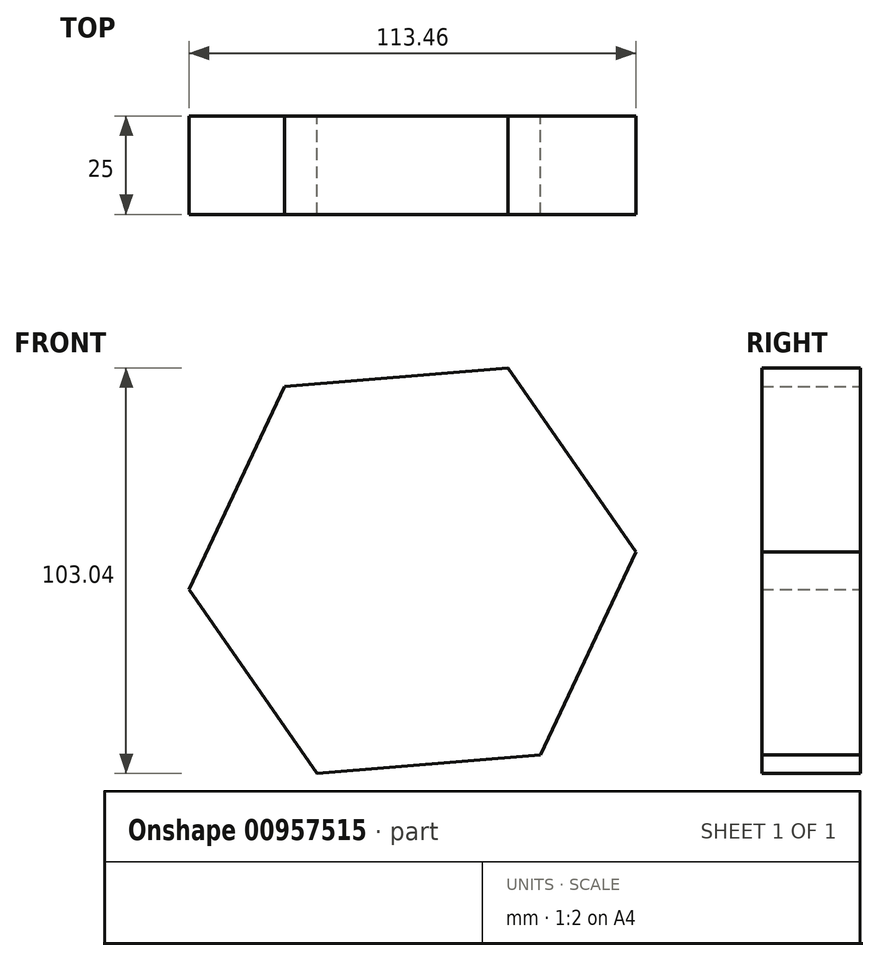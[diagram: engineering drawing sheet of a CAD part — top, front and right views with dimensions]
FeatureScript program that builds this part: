
annotation { "Feature Type Name" : "Feature", "Feature Type Description" : "" }
export const myFeature = defineFeature(function(context is Context, id is Id, definition is map)
    precondition{}
    {
        {
            var Q0;
            Q0=qCreatedBy(makeId("Front.planeOp"),FACE);
            var sketch = newSketch(context, id + "F0", { "sketchPlane" : qUnion([Q0])});
            skCircle(sketch, "E0.cCircle", {"center": v(0, 0) * mm, "radius": 49.3 * mm, "construction": true});
            skLineSegment(sketch, "E0.0", {"start": v(-32.5, 46.75) * mm, "end": v(24.23, 51.52) * mm});
            skLineSegment(sketch, "E0.1", {"start": v(24.23, 51.52) * mm, "end": v(56.73, 4.77) * mm});
            skLineSegment(sketch, "E0.2", {"start": v(56.73, 4.77) * mm, "end": v(32.5, -46.75) * mm});
            skLineSegment(sketch, "E0.3", {"start": v(32.5, -46.75) * mm, "end": v(-24.23, -51.52) * mm});
            skLineSegment(sketch, "E0.4", {"start": v(-24.23, -51.52) * mm, "end": v(-56.73, -4.77) * mm});
            skLineSegment(sketch, "E0.5", {"start": v(-56.73, -4.77) * mm, "end": v(-32.5, 46.75) * mm});
            skPoint(sketch, "E0.0.midPoint", {"position": v(-4.13, 49.13) * mm});
            skSolve(sketch);
        }
        {
            var Q0;
            Q0 = qSketchRegion(id + "F0", true);
            extrude(context, id + "F1", {"entities" : qUnion([Q0]), "depth" : 25 * mm, "offsetDistance" : 25 * mm});
        }
    });
